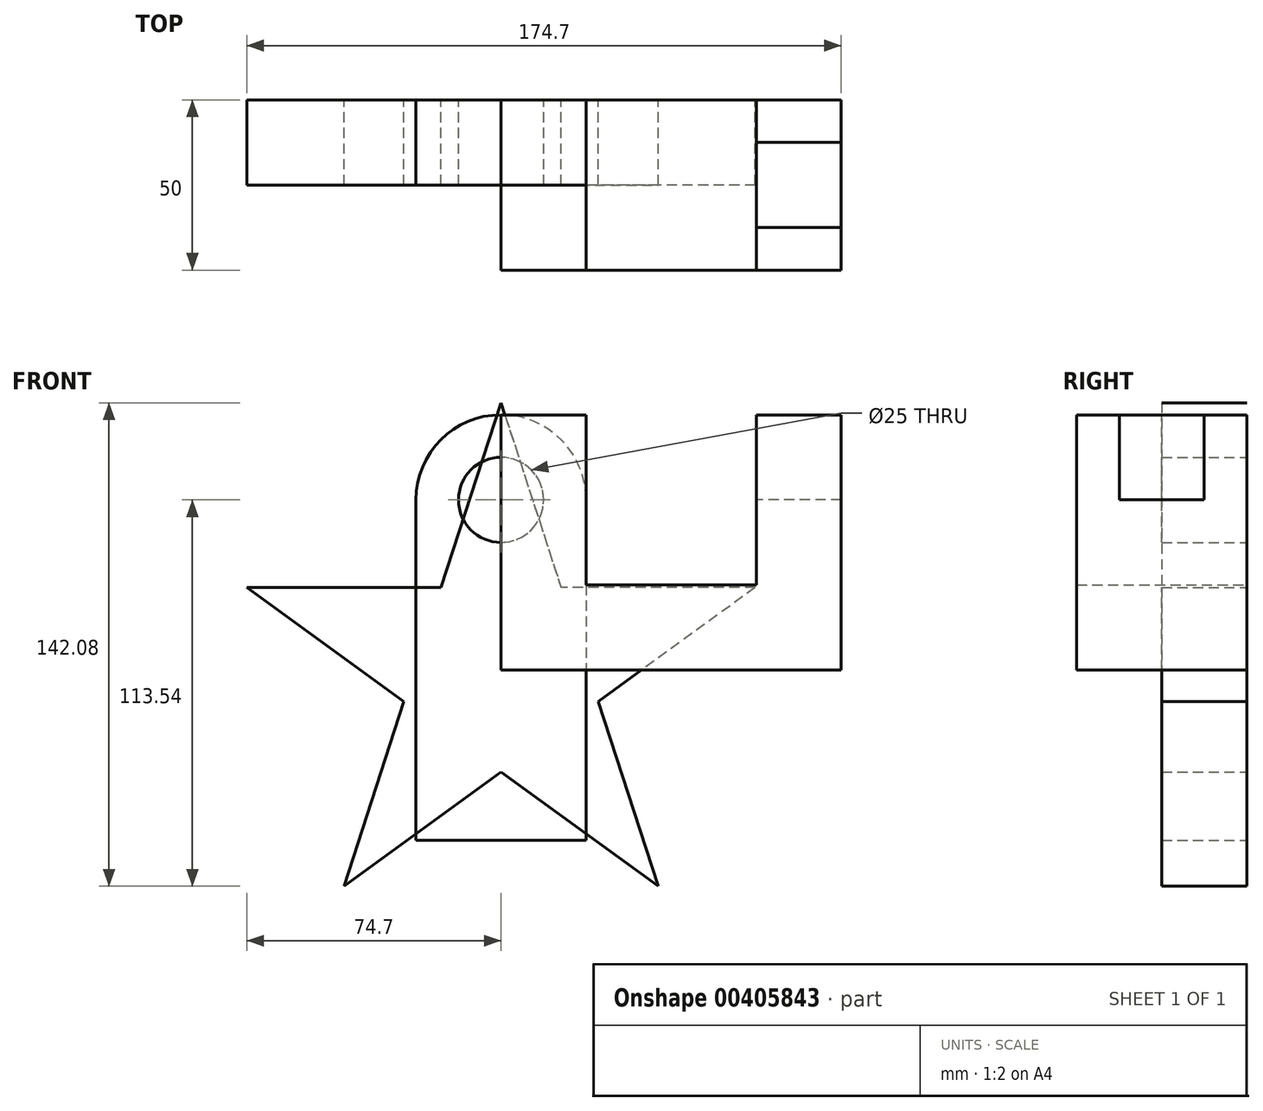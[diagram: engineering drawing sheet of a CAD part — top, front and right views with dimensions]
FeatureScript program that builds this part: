
annotation { "Feature Type Name" : "Feature", "Feature Type Description" : "" }
export const myFeature = defineFeature(function(context is Context, id is Id, definition is map)
    precondition{}
    {
        {
            var Q0;
            Q0=qCreatedBy(makeId("Front.planeOp"),FACE);
            var sketch = newSketch(context, id + "F0", { "sketchPlane" : qUnion([Q0])});
            skCircle(sketch, "E0.cCircle", {"center": v(0, 0) * mm, "radius": 63.54 * mm, "construction": true});
            skLineSegment(sketch, "E0.0", {"start": v(46.17, -63.54) * mm, "end": v(-46.17, -63.54) * mm, "construction": true});
            skLineSegment(sketch, "E0.1", {"start": v(-46.17, -63.54) * mm, "end": v(-74.7, 24.27) * mm, "construction": true});
            skLineSegment(sketch, "E0.2", {"start": v(-74.7, 24.27) * mm, "end": v(0, 78.54) * mm, "construction": true});
            skLineSegment(sketch, "E0.3", {"start": v(0, 78.54) * mm, "end": v(74.7, 24.27) * mm, "construction": true});
            skLineSegment(sketch, "E0.4", {"start": v(74.7, 24.27) * mm, "end": v(46.17, -63.54) * mm, "construction": true});
            skPoint(sketch, "E0.0.midPoint", {"position": v(0, -63.54) * mm});
            skLineSegment(sketch, "E1", {"start": v(0, -63.54) * mm, "end": v(0, 78.54) * mm, "construction": true});
            skLineSegment(sketch, "E2", {"start": v(-46.17, -63.54) * mm, "end": v(37.35, 51.4) * mm, "construction": true});
            skLineSegment(sketch, "E3", {"start": v(-74.7, 24.27) * mm, "end": v(60.43, -19.64) * mm, "construction": true});
            skLineSegment(sketch, "E4", {"start": v(74.7, 24.27) * mm, "end": v(-60.43, -19.64) * mm, "construction": true});
            skLineSegment(sketch, "E5", {"start": v(46.17, -63.54) * mm, "end": v(-37.35, 51.4) * mm, "construction": true});
            skLineSegment(sketch, "E6", {"start": v(0, 78.54) * mm, "end": v(-17.63, 24.27) * mm});
            skLineSegment(sketch, "E7", {"start": v(-17.63, 24.27) * mm, "end": v(-74.7, 24.27) * mm});
            skLineSegment(sketch, "E8", {"start": v(-28.53, -9.27) * mm, "end": v(-74.7, 24.27) * mm});
            skLineSegment(sketch, "E9", {"start": v(-46.17, -63.54) * mm, "end": v(-28.53, -9.27) * mm});
            skLineSegment(sketch, "E10", {"start": v(-46.17, -63.54) * mm, "end": v(0, -30) * mm});
            skLineSegment(sketch, "E11", {"start": v(0, -30) * mm, "end": v(46.17, -63.54) * mm});
            skLineSegment(sketch, "E12", {"start": v(46.17, -63.54) * mm, "end": v(28.53, -9.27) * mm});
            skLineSegment(sketch, "E13", {"start": v(74.7, 24.27) * mm, "end": v(28.53, -9.27) * mm});
            skLineSegment(sketch, "E14", {"start": v(74.7, 24.27) * mm, "end": v(17.63, 24.27) * mm});
            skLineSegment(sketch, "E15", {"start": v(0, 78.54) * mm, "end": v(17.63, 24.27) * mm});
            skCircle(sketch, "E16", {"center": v(0, 0) * mm, "radius": 30 * mm});
            skSolve(sketch);
        }
        {
            var Q0;
            {var subQ0=sQuery(id+"F0.wireOp",EDGE,"E7");Q0=makeQuery(id+"F0.imprint","IMPRINT",FACE,{"disambiguationData":[TD([[makeQuery(id+"F0.imprint","IMPRINT",EDGE,{"derivedFrom":subQ0}),1.0]])]});}
            var Q1;
            {var subQ0=sQuery(id+"F0.wireOp",EDGE,"E16");var subQ4=makeQuery(id+"F0.imprint","INTERSECT",VERTEX,{"derivedFrom":[sQuery(id+"F0.wireOp",EDGE,"E6"),sQuery(id+"F0.wireOp",EDGE,"E7"),subQ0]});Q1=makeQuery(id+"F0.imprint","IMPRINT",FACE,{"disambiguationData":[TD([[makeQuery(id+"F0.imprint","IMPRINT",EDGE,{"disambiguationData":[TD([[subQ4,1.0]])],"derivedFrom":subQ0}),1.0]])]});}
            var Q2;
            {var subQ0=sQuery(id+"F0.wireOp",EDGE,"E6");Q2=makeQuery(id+"F0.imprint","IMPRINT",FACE,{"disambiguationData":[TD([[makeQuery(id+"F0.imprint","IMPRINT",EDGE,{"derivedFrom":subQ0}),1.0]])]});}
            var Q3;
            {var subQ0=sQuery(id+"F0.wireOp",EDGE,"E13");Q3=makeQuery(id+"F0.imprint","IMPRINT",FACE,{"disambiguationData":[TD([[makeQuery(id+"F0.imprint","IMPRINT",EDGE,{"derivedFrom":subQ0}),-1.0]])]});}
            var Q4;
            {var subQ0=sQuery(id+"F0.wireOp",EDGE,"E11");Q4=makeQuery(id+"F0.imprint","IMPRINT",FACE,{"disambiguationData":[TD([[makeQuery(id+"F0.imprint","IMPRINT",EDGE,{"derivedFrom":subQ0}),1.0]])]});}
            var Q5;
            {var subQ0=sQuery(id+"F0.wireOp",EDGE,"E9");Q5=makeQuery(id+"F0.imprint","IMPRINT",FACE,{"disambiguationData":[TD([[makeQuery(id+"F0.imprint","IMPRINT",EDGE,{"derivedFrom":subQ0}),-1.0]])]});}
            extrude(context, id + "F1", {"entities" : qUnion([Q0, Q1, Q2, Q3, Q4, Q5]), "depth" : 25 * mm});
        }
        {
            var Q0;
            Q0=qCreatedBy(makeId("Front.planeOp"),FACE);
            var sketch = newSketch(context, id + "F2", { "sketchPlane" : qUnion([Q0])});
            skLineSegment(sketch, "E17.bottom", {"start": v(-25, 50) * mm, "end": v(25, 50) * mm});
            skLineSegment(sketch, "E17.top", {"start": v(-25, -50) * mm, "end": v(25, -50) * mm});
            skLineSegment(sketch, "E17.left", {"start": v(-25, 50) * mm, "end": v(-25, -50) * mm});
            skLineSegment(sketch, "E17.right", {"start": v(25, 50) * mm, "end": v(25, -50) * mm});
            skPoint(sketch, "E17.middle", {"position": v(0, 0) * mm});
            skCircle(sketch, "E18", {"center": v(0, 50) * mm, "radius": 25 * mm});
            skCircle(sketch, "E19", {"center": v(0, 50) * mm, "radius": 12.5 * mm});
            skSolve(sketch);
        }
        {
            var Q0;
            Q0=makeQuery(id+"F2.imprint","IMPRINT",FACE,{"disambiguationData":[TD([[makeQuery(id+"F2.imprint","IMPRINT",EDGE,{"derivedFrom":sQuery(id+"F2.wireOp",EDGE,"E17.top")}),1.0]])]});
            var Q1;
            {var subQ1=sQuery(id+"F2.wireOp",EDGE,"E17.bottom");var subQ3=sQuery(id+"F2.wireOp",EDGE,"E19");var subQ4=makeQuery(id+"F2.imprint","INTERSECT",VERTEX,{"disambiguationData":[OD(0.0)],"derivedFrom":[subQ1,subQ3]});Q1=makeQuery(id+"F2.imprint","IMPRINT",FACE,{"disambiguationData":[TD([[makeQuery(id+"F2.imprint","IMPRINT",EDGE,{"disambiguationData":[TD([[subQ4,-1.0]])],"derivedFrom":subQ3}),-1.0]])]});}
            var Q2;
            {var subQ1=sQuery(id+"F2.wireOp",EDGE,"E17.bottom");var subQ3=sQuery(id+"F2.wireOp",EDGE,"E19");var subQ4=makeQuery(id+"F2.imprint","INTERSECT",VERTEX,{"disambiguationData":[OD(0.0)],"derivedFrom":[subQ1,subQ3]});Q2=makeQuery(id+"F2.imprint","IMPRINT",FACE,{"disambiguationData":[TD([[makeQuery(id+"F2.imprint","IMPRINT",EDGE,{"disambiguationData":[TD([[subQ4,1.0]])],"derivedFrom":subQ3}),-1.0]])]});}
            extrude(context, id + "F3", {"entities" : qUnion([Q0, Q1, Q2]), "depth" : 25 * mm});
        }
        {
            var Q0;
            Q0=qCreatedBy(makeId("Front.planeOp"),FACE);
            var sketch = newSketch(context, id + "F4", { "sketchPlane" : qUnion([Q0])});
            skLineSegment(sketch, "E20.bottom", {"start": v(0, 0) * mm, "end": v(100, 0) * mm});
            skLineSegment(sketch, "E20.top", {"start": v(0, 75) * mm, "end": v(25, 75) * mm});
            skLineSegment(sketch, "E20.left", {"start": v(0, 0) * mm, "end": v(0, 75) * mm});
            skLineSegment(sketch, "E20.right", {"start": v(100, 0) * mm, "end": v(100, 75) * mm});
            skLineSegment(sketch, "E21.top", {"start": v(25, 25) * mm, "end": v(75, 25) * mm});
            skLineSegment(sketch, "E21.left", {"start": v(25, 75) * mm, "end": v(25, 25) * mm});
            skLineSegment(sketch, "E21.right", {"start": v(75, 75) * mm, "end": v(75, 25) * mm});
            skLineSegment(sketch, "E22.trimOffspring", {"start": v(75, 75) * mm, "end": v(100, 75) * mm});
            skSolve(sketch);
        }
        {
            var Q0;
            Q0=makeQuery(id+"F4.imprint","IMPRINT",FACE,{"disambiguationData":[TD([[makeQuery(id+"F4.imprint","IMPRINT",EDGE,{"derivedFrom":sQuery(id+"F4.wireOp",EDGE,"E20.bottom")}),1.0]])]});
            extrude(context, id + "F5", {"entities" : qUnion([Q0]), "depth" : 50 * mm});
        }
        {
            var Q0;
            Q0=makeQuery(id+"F5.opExtrude","SWEPT_FACE",FACE,{"disambiguationData":[OSD([sQuery(id+"F4.wireOp",EDGE,"E22.trimOffspring")])]});
            var sketch = newSketch(context, id + "F6", { "sketchPlane" : qUnion([Q0])});
            skLineSegment(sketch, "E23.bottom", {"start": v(100, -37.5) * mm, "end": v(75, -37.5) * mm});
            skLineSegment(sketch, "E23.top", {"start": v(100, -12.5) * mm, "end": v(75, -12.5) * mm});
            skLineSegment(sketch, "E23.left", {"start": v(100, -37.5) * mm, "end": v(100, -12.5) * mm});
            skLineSegment(sketch, "E23.right", {"start": v(75, -37.5) * mm, "end": v(75, -12.5) * mm});
            skSolve(sketch);
        }
        {
            var Q0;
            Q0=makeQuery(id+"F6.imprint","IMPRINT",FACE,{"disambiguationData":[TD([[makeQuery(id+"F6.imprint","IMPRINT",EDGE,{"derivedFrom":sQuery(id+"F6.wireOp",EDGE,"E23.bottom")}),-1.0]])]});
            extrude(context, id + "F7", {"entities" : qUnion([Q0]), "operationType" : NewBodyOperationType.REMOVE, "oppositeDirection" : true, "depth" : 25 * mm});
        }
    });
